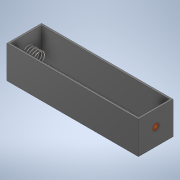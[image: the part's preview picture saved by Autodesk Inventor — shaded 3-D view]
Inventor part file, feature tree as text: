
AUTODESK INVENTOR PART (.ipt)
format: ipt  version: 2020 (Build 240168000, 168)  size: 329,216 bytes
history: native  units: mm
features: sketch x20, other x6, extrude x6, plane x4
ambient origin geometry x8: Origin, YZ Plane, XZ Plane, XY Plane, X Axis, Y Axis, Z Axis, Center Point
bodies: Body1 (feature_tree)
feature tree (36):
  other  "Sólido1"
  extrude  "Extrusión1"  Depth=19.75mm
  extrude  "Extrusión2"  Depth=38.5mm
  plane  "Plano de trabajo2"
  other  "Bobina1"
  plane  "Plano de trabajo3"
  plane  "Plano de trabajo4"
  plane  "Plano de trabajo5"
  other  "Bobina2"
  other  "Bobina3"
  other  "Bobina4"
  extrude  "Extrusión3"  Depth=1.0mm
  extrude  "Extrusión4"  Depth=1.0mm
  sketch  "Boceto10"  dims[d38=9.0mm]
  sketch  "Boceto11"  dims[d39=9.0mm]
  sketch  "Boceto12"  dims[d40=9.0mm]
  sketch  "Boceto13"  dims[d41=0.0mm d42=0.0mm d43=90.0deg d44=90.0deg d45=0.0mm d46=50.0mm d47=8.0mm d48=10.0mm]
  sketch  "Boceto14"  dims[d49=4.0mm d50=0.5mm]
  sketch  "Boceto15"  dims[d51=0.0mm d52=0.0mm d53=90.0deg d54=90.0deg d55=0.0mm d56=50.0mm d57=8.0mm d58=10.0mm]
  extrude  "Extrusión5"  Depth=1.0mm TaperAngle=0.0deg
  sketch  "Boceto17"  dims[d61=0.0mm d62=0.0mm d63=90.0deg d64=90.0deg d65=0.0mm d66=50.0mm d67=8.0mm d68=10.0mm]
  sketch  "Boceto18"  dims[d69=4.0mm d70=0.5mm]
  sketch  "Boceto19"  dims[d71=1.5mm]
  sketch  "Boceto20"  dims[d72=1.5mm]
  extrude  "Extrusión6"  Depth=9.0mm
  sketch  "Boceto1"  dims[d2=19.75mm d3=19.75mm]
  sketch  "Boceto2"  dims[d4=19.75mm d6=38.5mm]
  sketch  "Boceto4"  dims[d10=0.5mm d17=1.0mm d18=1.0mm]
  sketch  "Boceto8"  dims[d29=4.0mm]
  sketch  "Boceto9"  dims[d30=10.0mm d31=8.0mm d32=50.0mm d33=0.0mm d34=90.0deg d35=90.0deg d36=0.0mm d37=0.0mm]
  sketch  "Boceto16"  dims[d59=4.0mm d60=0.5mm]
  sketch  "Boceto21"  dims[d73=3.0mm d74=2.0mm d75=0.25mm d76=0.0mm d77=4.0mm d78=4.0mm d79=4.0mm d80=4.0mm d81=9.0mm d82=9.125mm d83=9.125mm d84=9.125mm d85=9.125mm d86=0.25mm d87=0.0mm d88=3.0mm d89=4.0mm d90=0.25mm d91=0.0mm d92=67.0mm d93=0.0mm]
  sketch  "Boceto5"  dims[d19=1.0mm d20=1.0mm]
  sketch  "Boceto6"  dims[d21=18.0mm d22=0.0mm d23=1.0mm d24=0.0mm]
  sketch  "Boceto7"  dims[d27=9.0mm d28=0.5mm]
  other  "Proyectar aristas de corte1"
